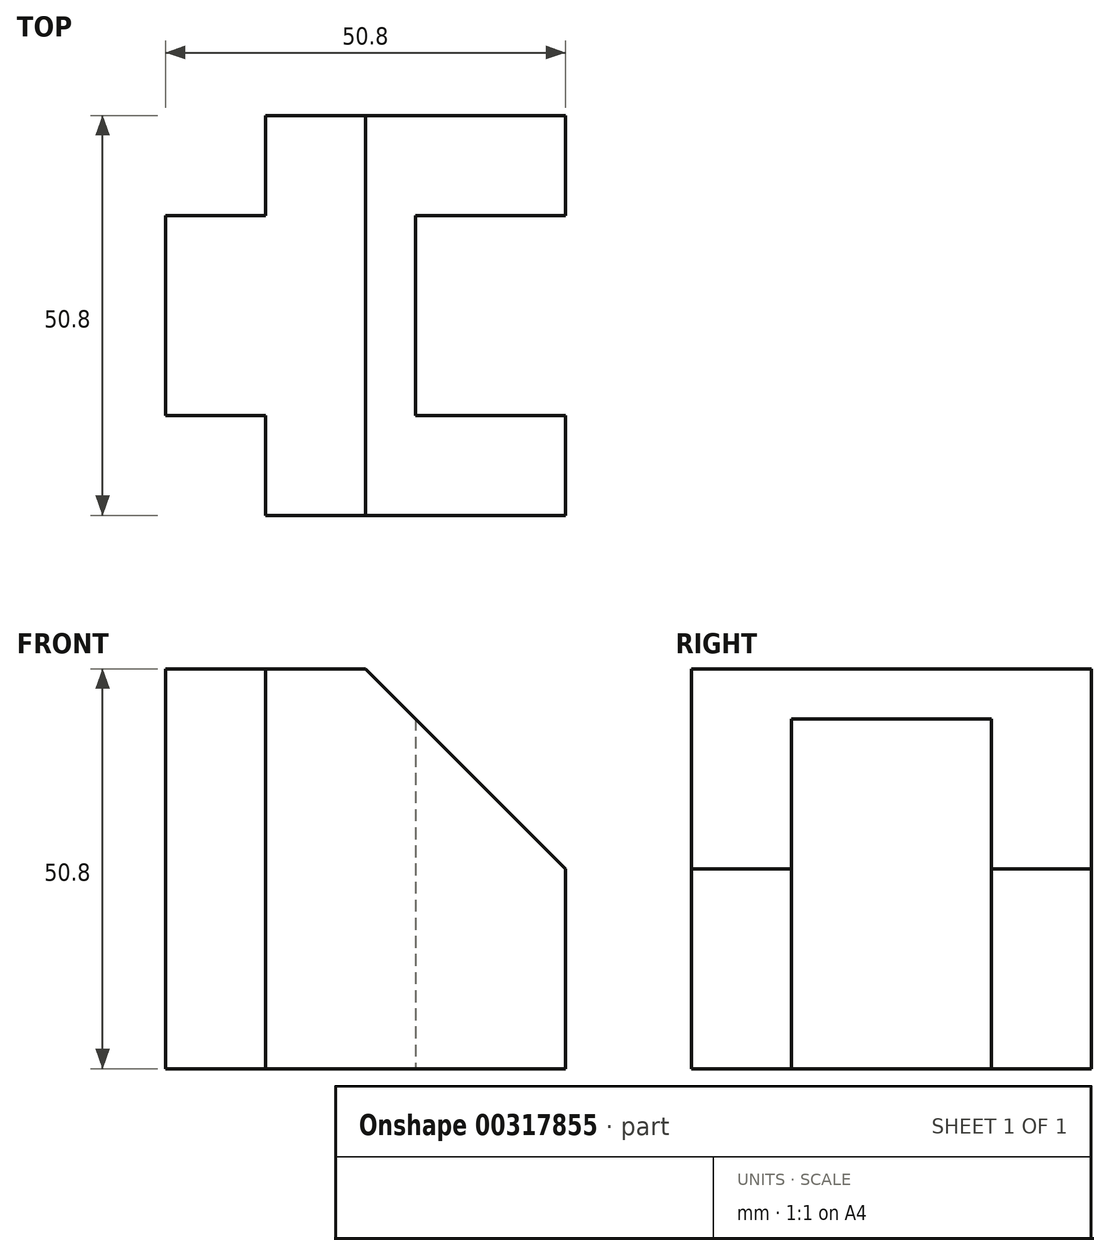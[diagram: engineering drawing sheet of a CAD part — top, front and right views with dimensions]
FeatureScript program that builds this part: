
annotation { "Feature Type Name" : "Feature", "Feature Type Description" : "" }
export const myFeature = defineFeature(function(context is Context, id is Id, definition is map)
    precondition{}
    {
        {
            var Q0;
            Q0=qCreatedBy(makeId("Top.planeOp"),FACE);
            var sketch = newSketch(context, id + "F0", { "sketchPlane" : qUnion([Q0])});
            skLineSegment(sketch, "E0", {"start": v(0, 12.7) * mm, "end": v(0, 38.1) * mm});
            skLineSegment(sketch, "E1", {"start": v(0, 38.1) * mm, "end": v(12.7, 38.1) * mm});
            skLineSegment(sketch, "E2", {"start": v(12.7, 38.1) * mm, "end": v(12.7, 50.8) * mm});
            skLineSegment(sketch, "E3", {"start": v(12.7, 0) * mm, "end": v(12.7, 12.7) * mm});
            skLineSegment(sketch, "E4", {"start": v(12.7, 12.7) * mm, "end": v(0, 12.7) * mm});
            skLineSegment(sketch, "E5", {"start": v(25.4, 0) * mm, "end": v(25.4, 50.8) * mm});
            skLineSegment(sketch, "E6", {"start": v(25.4, 50.8) * mm, "end": v(12.7, 50.8) * mm});
            skLineSegment(sketch, "E7", {"start": v(12.7, 0) * mm, "end": v(25.4, 0) * mm});
            skLineSegment(sketch, "E8", {"start": v(25.4, 50.8) * mm, "end": v(25.4, 0) * mm});
            skLineSegment(sketch, "E9", {"start": v(25.4, 0) * mm, "end": v(50.8, 0) * mm});
            skLineSegment(sketch, "E10", {"start": v(50.8, 0) * mm, "end": v(50.8, 12.7) * mm});
            skLineSegment(sketch, "E11", {"start": v(50.8, 12.7) * mm, "end": v(31.75, 12.7) * mm});
            skLineSegment(sketch, "E12", {"start": v(31.75, 12.7) * mm, "end": v(31.75, 38.1) * mm});
            skLineSegment(sketch, "E13", {"start": v(31.75, 38.1) * mm, "end": v(50.8, 38.1) * mm});
            skLineSegment(sketch, "E14", {"start": v(50.8, 38.1) * mm, "end": v(50.8, 50.8) * mm});
            skLineSegment(sketch, "E15", {"start": v(50.8, 50.8) * mm, "end": v(25.4, 50.8) * mm});
            skSolve(sketch);
        }
        {
            var Q0;
            Q0 = qSketchRegion(id + "F0", true);
            extrude(context, id + "F1", {"entities" : qUnion([Q0]), "depth" : 50.8 * mm});
        }
        {
            var Q0;
            Q0=makeQuery(id+"F1.opExtrude","SWEPT_FACE",FACE,{"disambiguationData":[OSD([sQuery(id+"F0.wireOp",EDGE,"E7"),sQuery(id+"F0.wireOp",EDGE,"E9")])]});
            var sketch = newSketch(context, id + "F2", { "sketchPlane" : qUnion([Q0])});
            skLineSegment(sketch, "E16", {"start": v(50.8, 50.8) * mm, "end": v(50.8, 25.4) * mm});
            skLineSegment(sketch, "E17", {"start": v(50.8, 25.4) * mm, "end": v(25.4, 50.8) * mm});
            skLineSegment(sketch, "E18", {"start": v(25.4, 50.8) * mm, "end": v(50.8, 50.8) * mm});
            skSolve(sketch);
        }
        {
            var Q0;
            Q0 = qSketchRegion(id + "F2", true);
            extrude(context, id + "F3", {"entities" : qUnion([Q0]), "operationType" : NewBodyOperationType.REMOVE, "endBound" : BoundingType.THROUGH_ALL, "oppositeDirection" : true, "depth" : 25.4 * mm});
        }
    });
